# Revit family: Reece_Shower_Mizu_Drift_Shower Set_Gooseneck
name_source: partatom
category: Plumbing Fixtures
revit_build: Autodesk Revit 2018 (Build: 20190510_1515(x64)
units: mm (PartAtom-declared; Revit-internal decimal feet)

## family parameters
Always vertical = Yes
Cut with Voids When Loaded = Yes
Part Type = Normal
Room Calculation Point = Yes
Round Connector Dimension = Use Diameter
Shared = Yes
Work Plane-Based = Yes

## types (1)
- Chrome
    Default Elevation = 0 mm  [stored 0 ft]
    Description = Mizu Drift Gooseneck Shower Set 300mm Chrome (3 Star)
    Disclaimer = THIS FILE IS THE PROPERTY OF THE REECE GROUP. IT MAY NOT BE REPRODUCED, REVERSE-ENGINEERED OR MODIFIED. ANY REPUBLICATION, TRANSMISSION OR DISTRIBUTION FOR THE PURPOSE OF COMMERCIALLY EXPLOITING THE FILES IS PROHIBITED.
    Keynote = Product #9505993, Reece_Shower_Mizu_Drift_Shower Set_Gooseneck - Chrome
    Manufacturer = Mizu
    Model = Drift
    Reece_Assembly_High = 1000 mm  [stored 3.28084 ft]
    Reece_Detail_Additional = Gooseneck
    Reece_Detail_Disclaimer = THIS FILE IS THE PROPERTY OF THE REECE GROUP. IT MAY NOT BE REPRODUCED, REVERSE-ENGINEERED OR MODIFIED. ANY REPUBLICATION, TRANSMISSION OR DISTRIBUTION FOR THE PURPOSE OF COMMERCIALLY EXPLOITING THE FILES IS PROHIBITED.
    Reece_Material_Main = Reece_Brass_Chrome
    Reece_Offset = 75 mm  [stored 0.246063 ft]
    Reece_Offset_Distance = 75 mm  [stored 0.246063 ft]
    Reece_Overall-Diameter = 300 mm  [stored 0.984252 ft]
    Reece_Overall_Height = 380 mm
    Reece_Overall_Projection = 400 mm  [stored 1.31234 ft]
    Reece_Product_Brand = Mizu
    Reece_Product_Description = Mizu Drift Gooseneck Shower Set 300mm Chrome (3 Star)
    Reece_Product_Mount = Wall Mounted
    Reece_Product_Number = 9505993
    Reece_Product_Sub Brand = Drift
    Reece_Product_Type = Shower Set
    Reece_Product_Web Page = https://www.reece.com.au
    Reece_Shower_Inlet = 15 mm  [stored 0.0492126 ft]
    Reece_Shower_Reach = 334 mm  [stored 1.0958 ft]
    Type Comments = Shower Set
    URL = https://www.reece.com.au

note: [stored X ft] marks values corroborated as IEEE doubles in the binary element streams (Revit-internal decimal feet)

## geometry (parser evidence)
native form markers: Sweep x12
no freeform markers — native parametric forms only
